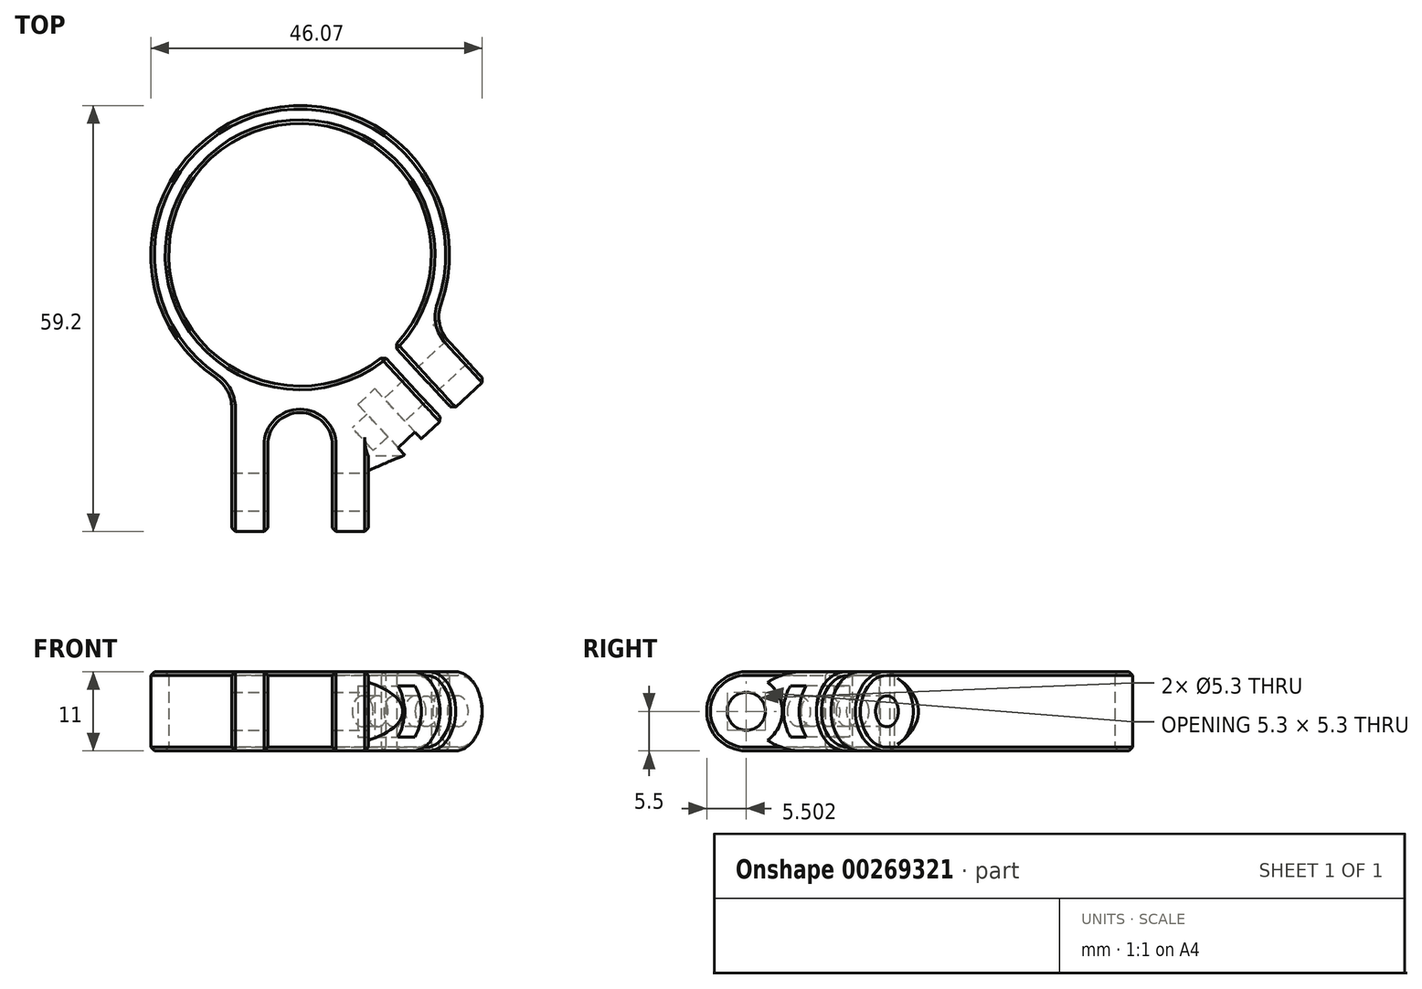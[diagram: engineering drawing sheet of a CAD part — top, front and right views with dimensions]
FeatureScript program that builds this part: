
annotation { "Feature Type Name" : "Feature", "Feature Type Description" : "" }
export const myFeature = defineFeature(function(context is Context, id is Id, definition is map)
    precondition{}
    {
        {
            var Q0;
            Q0=qCreatedBy(makeId("Top.planeOp"),FACE);
            var sketch = newSketch(context, id + "F0", { "sketchPlane" : qUnion([Q0])});
            skLineSegment(sketch, "E0.MirrorCS", {"start": v(-9.5, -18.45) * mm, "end": v(-9.5, -38.45) * mm});
            skLineSegment(sketch, "E1.MirrorCS", {"start": v(-9.5, -38.45) * mm, "end": v(-4.5, -38.45) * mm});
            skLineSegment(sketch, "E2.MirrorCS", {"start": v(-4.5, -38.45) * mm, "end": v(-4.5, -26.45) * mm});
            skArc(sketch, "E3.MirrorCS", {"start": v(-4.5, -26.45) * mm, "mid": v(0, -21.95) * mm, "end": v(4.5, -26.45) * mm});
            skLineSegment(sketch, "E4.MirrorCS", {"start": v(4.5, -26.45) * mm, "end": v(4.5, -38.45) * mm});
            skLineSegment(sketch, "E5.MirrorCS", {"start": v(4.5, -38.45) * mm, "end": v(9.5, -38.45) * mm});
            skLineSegment(sketch, "E6.MirrorCS", {"start": v(9.5, -38.45) * mm, "end": v(9.5, -32.38) * mm});
            skLineSegment(sketch, "E7.MirrorCS", {"start": v(19.78, -22.87) * mm, "end": v(9.5, -32.38) * mm});
            skLineSegment(sketch, "E8.MirrorCS", {"start": v(19.78, -22.87) * mm, "end": v(11.64, -14.06) * mm});
            skLineSegment(sketch, "E9.MirrorCS", {"start": v(13.1, -12.7) * mm, "end": v(21.25, -21.51) * mm});
            skLineSegment(sketch, "E10.MirrorCS", {"start": v(21.25, -21.51) * mm, "end": v(25.66, -17.44) * mm});
            skLineSegment(sketch, "E11.MirrorCS", {"start": v(25.66, -17.44) * mm, "end": v(18.4, -9.6) * mm});
            skArc(sketch, "E12", {"start": v(18.4, -9.6) * mm, "mid": v(-6.28, 19.78) * mm, "end": v(-9.5, -18.45) * mm});
            skArc(sketch, "E13", {"start": v(13.1, -12.7) * mm, "mid": v(-12.39, 13.4) * mm, "end": v(11.64, -14.06) * mm});
            skLineSegment(sketch, "E14", {"start": v(0, 0) * mm, "end": v(35.54, -38.45) * mm, "construction": true});
            skLineSegment(sketch, "E15", {"start": v(0, 0) * mm, "end": v(0, -26.45) * mm, "construction": true});
            skSolve(sketch);
        }
        {
            var Q0;
            Q0=qSketchRegion(id+"F0",true);
            extrude(context, id + "F1", {"entities" : qUnion([Q0]), "endBound" : BoundingType.SYMMETRIC, "depth" : 11 * mm});
        }
        {
            var Q0;
            Q0=makeQuery(id+"F1.opExtrude","SWEPT_FACE",FACE,{"disambiguationData":[OSD([sQuery(id+"F0.wireOp",EDGE,"E7.MirrorCS")])]});
            var sketch = newSketch(context, id + "F2", { "sketchPlane" : qUnion([Q0])});
            skLineSegment(sketch, "E16", {"start": v(-1, 0) * mm, "end": v(-15, 0) * mm, "construction": true});
            skLineSegment(sketch, "E17.bottom", {"start": v(-8.2, 3.55) * mm, "end": v(-5, 3.55) * mm});
            skLineSegment(sketch, "E17.top", {"start": v(-8.2, -3.55) * mm, "end": v(-5, -3.55) * mm});
            skLineSegment(sketch, "E17.left", {"start": v(-8.2, 3.55) * mm, "end": v(-8.2, -3.55) * mm});
            skLineSegment(sketch, "E17.right", {"start": v(-5, 3.55) * mm, "end": v(-5, -3.55) * mm});
            skPoint(sketch, "E17.middle", {"position": v(-6.6, 0) * mm});
            skSolve(sketch);
        }
        {
            var Q0;
            Q0=qSketchRegion(id+"F2",true);
            extrude(context, id + "F3", {"entities" : qUnion([Q0]), "operationType" : NewBodyOperationType.REMOVE, "oppositeDirection" : true, "depth" : 9.5 * mm});
        }
        {
            var Q0;
            Q0=makeQuery(id+"F1.opExtrude","SWEPT_EDGE",EDGE,{"disambiguationData":[OSD([sQuery(id+"F0.wireOp",EDGE,"E0.MirrorCS"),sQuery(id+"F0.wireOp",EDGE,"E12")])]});
            var Q1;
            Q1=makeQuery(id+"F1.opExtrude","SWEPT_EDGE",EDGE,{"disambiguationData":[OSD([sQuery(id+"F0.wireOp",EDGE,"E11.MirrorCS"),sQuery(id+"F0.wireOp",EDGE,"E12")])]});
            fillet(context, id + "F4", {"entities" : qUnion([Q0, Q1]), "radius" : 5 * mm, "tangentPropagation" : true, "allowEdgeOverflow" : false});
        }
        {
            var Q0;
            Q0=makeQuery(id+"F1.opExtrude","CAP_EDGE",EDGE,{"disambiguationData":[OSD([sQuery(id+"F0.wireOp",EDGE,"E10.MirrorCS")])],"isStart":false});
            var Q1;
            Q1=makeQuery(id+"F1.opExtrude","CAP_EDGE",EDGE,{"disambiguationData":[OSD([sQuery(id+"F0.wireOp",EDGE,"E10.MirrorCS")])],"isStart":true});
            var Q2;
            Q2=makeQuery(id+"F1.opExtrude","CAP_EDGE",EDGE,{"disambiguationData":[OSD([sQuery(id+"F0.wireOp",EDGE,"E5.MirrorCS")])],"isStart":false});
            var Q3;
            Q3=makeQuery(id+"F1.opExtrude","CAP_EDGE",EDGE,{"disambiguationData":[OSD([sQuery(id+"F0.wireOp",EDGE,"E1.MirrorCS")])],"isStart":false});
            var Q4;
            Q4=makeQuery(id+"F1.opExtrude","CAP_EDGE",EDGE,{"disambiguationData":[OSD([sQuery(id+"F0.wireOp",EDGE,"E5.MirrorCS")])],"isStart":true});
            var Q5;
            Q5=makeQuery(id+"F1.opExtrude","CAP_EDGE",EDGE,{"disambiguationData":[OSD([sQuery(id+"F0.wireOp",EDGE,"E1.MirrorCS")])],"isStart":true});
            var Q6;
            Q6=makeQuery(id+"F1.opExtrude","CAP_EDGE",EDGE,{"disambiguationData":[OSD([sQuery(id+"F0.wireOp",EDGE,"E7.MirrorCS")])],"isStart":false});
            var Q7;
            Q7=makeQuery(id+"F1.opExtrude","CAP_EDGE",EDGE,{"disambiguationData":[OSD([sQuery(id+"F0.wireOp",EDGE,"E7.MirrorCS")])],"isStart":true});
            fillet(context, id + "F5", {"entities" : qUnion([Q0, Q1, Q2, Q3, Q4, Q5, Q6, Q7]), "radius" : 5.5 * mm, "tangentPropagation" : true, "allowEdgeOverflow" : false});
        }
        {
            var Q0;
            Q0=makeQuery(id+"F1.opExtrude","SWEPT_FACE",FACE,{"disambiguationData":[OSD([sQuery(id+"F0.wireOp",EDGE,"E6.MirrorCS")])]});
            var sketch = newSketch(context, id + "F6", { "sketchPlane" : qUnion([Q0])});
            skCircle(sketch, "E18", {"center": v(-32.95, 0) * mm, "radius": 2.65 * mm});
            skSolve(sketch);
        }
        {
            var Q0;
            Q0=qSketchRegion(id+"F6",true);
            var Q1;
            Q1=makeQuery(id+"F1.opExtrude","SWEPT_FACE",FACE,{"disambiguationData":[OSD([sQuery(id+"F0.wireOp",EDGE,"E0.MirrorCS")])]});
            var Q2;
            Q2=makeQuery(id+"F1.opExtrude","SWEPT_FACE",FACE,{"disambiguationData":[OSD([sQuery(id+"F0.wireOp",EDGE,"E8.MirrorCS")])]});
            extrude(context, id + "F7", {"entities" : qUnion([Q0]), "operationType" : NewBodyOperationType.REMOVE, "endBound" : BoundingType.UP_TO_SURFACE, "oppositeDirection" : true, "endBoundEntityFace" : qUnion([Q1]), "depth" : 50 * mm, "hasSecondDirection" : true, "secondDirectionBound" : SecondDirectionBoundingType.UP_TO_SURFACE, "secondDirectionOppositeDirection" : false, "secondDirectionBoundEntityFace" : qUnion([Q2]), "secondDirectionDepth" : 25 * mm});
        }
        {
            var Q0;
            Q0=makeQuery(id+"F1.opExtrude","SWEPT_FACE",FACE,{"disambiguationData":[OSD([sQuery(id+"F0.wireOp",EDGE,"E6.MirrorCS")])]});
            var sketch = newSketch(context, id + "F8", { "sketchPlane" : qUnion([Q0])});
            skCircle(sketch, "E19", {"center": v(-32.95, 0) * mm, "radius": 5 * mm});
            skSolve(sketch);
        }
        {
            var Q0;
            Q0=qSketchRegion(id+"F8",true);
            var Q1;
            Q1=makeQuery(id+"F1.opExtrude","SWEPT_FACE",FACE,{"disambiguationData":[OSD([sQuery(id+"F0.wireOp",EDGE,"E8.MirrorCS")])]});
            extrude(context, id + "F9", {"entities" : qUnion([Q0]), "operationType" : NewBodyOperationType.REMOVE, "endBound" : BoundingType.UP_TO_SURFACE, "endBoundEntityFace" : qUnion([Q1]), "depth" : 25 * mm});
        }
        {
            var Q0;
            Q0=makeQuery(id+"F1.opExtrude","SWEPT_FACE",FACE,{"disambiguationData":[OSD([sQuery(id+"F0.wireOp",EDGE,"E9.MirrorCS")])]});
            var Q1;
            Q1=makeQuery(id+"F1.opExtrude","SWEPT_FACE",FACE,{"disambiguationData":[OSD([sQuery(id+"F0.wireOp",EDGE,"E8.MirrorCS")])]});
            cPlane(context, id + "F10", {"entities" : qUnion([Q0, Q1]), "cplaneType" : CPlaneType.MID_PLANE, "offset" : 25 * mm, "width" : 150 * mm, "height" : 150 * mm});
        }
        {
            var Q0;
            Q0=qCreatedBy(id+"F10.planeOp",FACE);
            var sketch = newSketch(context, id + "F11", { "sketchPlane" : qUnion([Q0])});
            skCircle(sketch, "E20", {"center": v(24.72, 0) * mm, "radius": 2.15 * mm});
            skSolve(sketch);
        }
        {
            var Q0;
            Q0=qSketchRegion(id+"F11",true);
            var Q1;
            Q1=makeQuery(id+"F1.opExtrude","SWEPT_FACE",FACE,{"disambiguationData":[OSD([sQuery(id+"F0.wireOp",EDGE,"E11.MirrorCS")])]});
            var Q2;
            {var subQ0=sQuery(id+"F0.wireOp",EDGE,"E12");var subQ1=sQuery(id+"F0.wireOp",EDGE,"E11.MirrorCS");Q2=makeQuery(id+"F4.opFillet","BLEND_VERTEX",VERTEX,{"blendedFrom":[makeQuery(id+"F1.opExtrude","SWEPT_EDGE",EDGE,{"disambiguationData":[OSD([subQ1,subQ0])]}),makeQuery(id+"F1.opExtrude","CAP_FACE",FACE,{"disambiguationData":[OSD([sQuery(id+"F0.wireOp",EDGE,"E0.MirrorCS"),sQuery(id+"F0.wireOp",EDGE,"E1.MirrorCS"),sQuery(id+"F0.wireOp",EDGE,"E2.MirrorCS"),sQuery(id+"F0.wireOp",EDGE,"E3.MirrorCS"),sQuery(id+"F0.wireOp",EDGE,"E4.MirrorCS"),sQuery(id+"F0.wireOp",EDGE,"E5.MirrorCS"),sQuery(id+"F0.wireOp",EDGE,"E6.MirrorCS"),sQuery(id+"F0.wireOp",EDGE,"E7.MirrorCS"),sQuery(id+"F0.wireOp",EDGE,"E8.MirrorCS"),sQuery(id+"F0.wireOp",EDGE,"E9.MirrorCS"),sQuery(id+"F0.wireOp",EDGE,"E10.MirrorCS"),subQ1,subQ0,sQuery(id+"F0.wireOp",EDGE,"E13")])],"isStart":true}),makeQuery(id+"F1.opExtrude","SWEPT_FACE",FACE,{"disambiguationData":[OSD([subQ0])]})],"blendedInto":[makeQuery(id+"F1.opExtrude","CAP_FACE",FACE,{"disambiguationData":[OSD([sQuery(id+"F0.wireOp",EDGE,"E0.MirrorCS"),sQuery(id+"F0.wireOp",EDGE,"E1.MirrorCS"),sQuery(id+"F0.wireOp",EDGE,"E2.MirrorCS"),sQuery(id+"F0.wireOp",EDGE,"E3.MirrorCS"),sQuery(id+"F0.wireOp",EDGE,"E4.MirrorCS"),sQuery(id+"F0.wireOp",EDGE,"E5.MirrorCS"),sQuery(id+"F0.wireOp",EDGE,"E6.MirrorCS"),sQuery(id+"F0.wireOp",EDGE,"E7.MirrorCS"),sQuery(id+"F0.wireOp",EDGE,"E8.MirrorCS"),sQuery(id+"F0.wireOp",EDGE,"E9.MirrorCS"),sQuery(id+"F0.wireOp",EDGE,"E10.MirrorCS"),subQ1,subQ0,sQuery(id+"F0.wireOp",EDGE,"E13")])],"isStart":true}),makeQuery(id+"F1.opExtrude","SWEPT_FACE",FACE,{"disambiguationData":[OSD([subQ0])]})]});}
            extrude(context, id + "F12", {"entities" : qUnion([Q0]), "operationType" : NewBodyOperationType.REMOVE, "endBound" : BoundingType.UP_TO_VERTEX, "oppositeDirection" : true, "endBoundEntityFace" : qUnion([Q1]), "endBoundEntityVertex" : qUnion([Q2]), "depth" : 25 * mm, "hasSecondDirection" : true, "secondDirectionOppositeDirection" : false, "secondDirectionDepth" : 11 * mm});
        }
        {
            var Q0;
            Q0=makeQuery(id+"F1.opExtrude","SWEPT_FACE",FACE,{"disambiguationData":[OSD([sQuery(id+"F0.wireOp",EDGE,"E11.MirrorCS")])]});
            var sketch = newSketch(context, id + "F13", { "sketchPlane" : qUnion([Q0])});
            skCircle(sketch, "E21", {"center": v(-24.72, 0) * mm, "radius": 5 * mm});
            skSolve(sketch);
        }
        {
            var Q0;
            Q0=qSketchRegion(id+"F13",true);
            var Q1;
            {var subQ0=sQuery(id+"F0.wireOp",EDGE,"E12");var subQ1=sQuery(id+"F0.wireOp",EDGE,"E11.MirrorCS");Q1=makeQuery(id+"F4.opFillet","BLEND_VERTEX",VERTEX,{"blendedFrom":[makeQuery(id+"F1.opExtrude","SWEPT_EDGE",EDGE,{"disambiguationData":[OSD([subQ1,subQ0])]}),makeQuery(id+"F1.opExtrude","CAP_FACE",FACE,{"disambiguationData":[OSD([sQuery(id+"F0.wireOp",EDGE,"E0.MirrorCS"),sQuery(id+"F0.wireOp",EDGE,"E1.MirrorCS"),sQuery(id+"F0.wireOp",EDGE,"E2.MirrorCS"),sQuery(id+"F0.wireOp",EDGE,"E3.MirrorCS"),sQuery(id+"F0.wireOp",EDGE,"E4.MirrorCS"),sQuery(id+"F0.wireOp",EDGE,"E5.MirrorCS"),sQuery(id+"F0.wireOp",EDGE,"E6.MirrorCS"),sQuery(id+"F0.wireOp",EDGE,"E7.MirrorCS"),sQuery(id+"F0.wireOp",EDGE,"E8.MirrorCS"),sQuery(id+"F0.wireOp",EDGE,"E9.MirrorCS"),sQuery(id+"F0.wireOp",EDGE,"E10.MirrorCS"),subQ1,subQ0,sQuery(id+"F0.wireOp",EDGE,"E13")])],"isStart":true}),makeQuery(id+"F1.opExtrude","SWEPT_FACE",FACE,{"disambiguationData":[OSD([subQ0])]})],"blendedInto":[makeQuery(id+"F1.opExtrude","CAP_FACE",FACE,{"disambiguationData":[OSD([sQuery(id+"F0.wireOp",EDGE,"E0.MirrorCS"),sQuery(id+"F0.wireOp",EDGE,"E1.MirrorCS"),sQuery(id+"F0.wireOp",EDGE,"E2.MirrorCS"),sQuery(id+"F0.wireOp",EDGE,"E3.MirrorCS"),sQuery(id+"F0.wireOp",EDGE,"E4.MirrorCS"),sQuery(id+"F0.wireOp",EDGE,"E5.MirrorCS"),sQuery(id+"F0.wireOp",EDGE,"E6.MirrorCS"),sQuery(id+"F0.wireOp",EDGE,"E7.MirrorCS"),sQuery(id+"F0.wireOp",EDGE,"E8.MirrorCS"),sQuery(id+"F0.wireOp",EDGE,"E9.MirrorCS"),sQuery(id+"F0.wireOp",EDGE,"E10.MirrorCS"),subQ1,subQ0,sQuery(id+"F0.wireOp",EDGE,"E13")])],"isStart":true}),makeQuery(id+"F1.opExtrude","SWEPT_FACE",FACE,{"disambiguationData":[OSD([subQ0])]})]});}
            extrude(context, id + "F14", {"entities" : qUnion([Q0]), "operationType" : NewBodyOperationType.REMOVE, "endBound" : BoundingType.UP_TO_VERTEX, "endBoundEntityVertex" : qUnion([Q1]), "depth" : 25 * mm});
        }
        {
            var Q0;
            Q0=makeQuery(id+"F1.opExtrude","CAP_FACE",FACE,{"disambiguationData":[OSD([sQuery(id+"F0.wireOp",EDGE,"E0.MirrorCS"),sQuery(id+"F0.wireOp",EDGE,"E1.MirrorCS"),sQuery(id+"F0.wireOp",EDGE,"E2.MirrorCS"),sQuery(id+"F0.wireOp",EDGE,"E3.MirrorCS"),sQuery(id+"F0.wireOp",EDGE,"E4.MirrorCS"),sQuery(id+"F0.wireOp",EDGE,"E5.MirrorCS"),sQuery(id+"F0.wireOp",EDGE,"E6.MirrorCS"),sQuery(id+"F0.wireOp",EDGE,"E7.MirrorCS"),sQuery(id+"F0.wireOp",EDGE,"E8.MirrorCS"),sQuery(id+"F0.wireOp",EDGE,"E9.MirrorCS"),sQuery(id+"F0.wireOp",EDGE,"E10.MirrorCS"),sQuery(id+"F0.wireOp",EDGE,"E11.MirrorCS"),sQuery(id+"F0.wireOp",EDGE,"E12"),sQuery(id+"F0.wireOp",EDGE,"E13")])],"isStart":true});
            var Q1;
            Q1=makeQuery(id+"F1.opExtrude","SWEPT_EDGE",EDGE,{"disambiguationData":[OSD([sQuery(id+"F0.wireOp",EDGE,"E8.MirrorCS"),sQuery(id+"F0.wireOp",EDGE,"E13")])]});
            var Q2;
            Q2=makeQuery(id+"F1.opExtrude","SWEPT_EDGE",EDGE,{"disambiguationData":[OSD([sQuery(id+"F0.wireOp",EDGE,"E9.MirrorCS"),sQuery(id+"F0.wireOp",EDGE,"E13")])]});
            var Q3;
            Q3=makeQuery(id+"F1.opExtrude","CAP_EDGE",EDGE,{"disambiguationData":[OSD([sQuery(id+"F0.wireOp",EDGE,"E13")])],"isStart":false});
            chamfer(context, id + "F15", {"entities" : qUnion([Q0, Q1, Q2, Q3]), "width" : 0.5 * mm, "tangentPropagation" : true});
        }
    });
